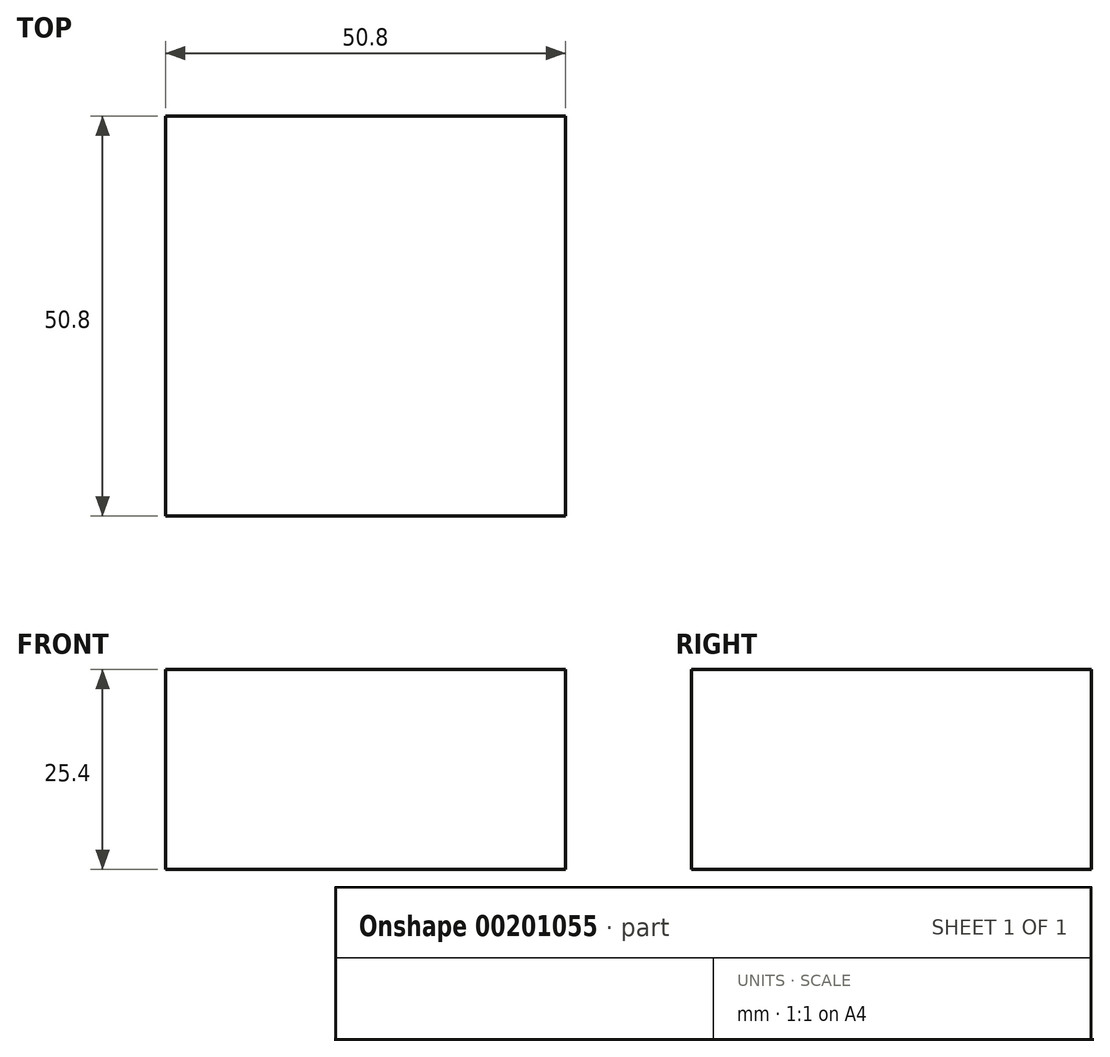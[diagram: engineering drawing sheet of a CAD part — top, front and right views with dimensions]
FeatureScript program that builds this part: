
annotation { "Feature Type Name" : "Feature", "Feature Type Description" : "" }
export const myFeature = defineFeature(function(context is Context, id is Id, definition is map)
    precondition{}
    {
        {
            var Q0;
            Q0=qCreatedBy(makeId("Top.planeOp"),FACE);
            var sketch = newSketch(context, id + "F0", { "sketchPlane" : qUnion([Q0])});
            skLineSegment(sketch, "E0.bottom", {"start": v(-25.4, 25.4) * mm, "end": v(25.4, 25.4) * mm});
            skLineSegment(sketch, "E0.top", {"start": v(-25.4, -25.4) * mm, "end": v(25.4, -25.4) * mm});
            skLineSegment(sketch, "E0.left", {"start": v(-25.4, 25.4) * mm, "end": v(-25.4, -25.4) * mm});
            skLineSegment(sketch, "E0.right", {"start": v(25.4, 25.4) * mm, "end": v(25.4, -25.4) * mm});
            skPoint(sketch, "E0.middle", {"position": v(0, 0) * mm});
            skSolve(sketch);
        }
        {
            var Q0;
            Q0 = qSketchRegion(id + "F0", true);
            extrude(context, id + "F1", {"entities" : qUnion([Q0]), "depth" : 25.4 * mm});
        }
    });
